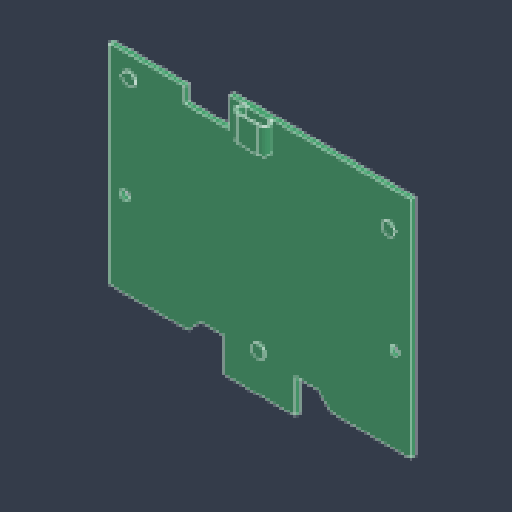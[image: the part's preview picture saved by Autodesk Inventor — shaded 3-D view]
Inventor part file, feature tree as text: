
AUTODESK INVENTOR PART (.ipt)
format: ipt  version: 2023.4 (Build 274418000, 418)  size: 162,816 bytes
history: native  units: mm
features: sketch x4, extrude x3, hole x1
ambient origin geometry x8: Origin, YZ Plane, XZ Plane, XY Plane, X Axis, Y Axis, Z Axis, Center Point
bodies: Solid1 (feature_tree)
feature tree (8):
  extrude  "Extrusion1"  Depth=65.0mm
  hole  "Hole1"  [1 undecoded]
  extrude  "Extrusion2"  Depth=3.5mm
  extrude  "Extrusion3"  TaperAngle=45.0deg  [1 undecoded]
  sketch  "Sketch1"  dims[d0=80.0mm d1=65.0mm]
  sketch  "Sketch2"  dims[d2=19.0mm d3=45.0deg]
  sketch  "Sketch4"  dims[d4=9.0mm d5=3.5mm]
  sketch  "Sketch5"  dims[d6=6.0mm d7=45.0deg d8=8.0mm d9=8.0mm d10=12.0mm d11=4.0mm d12=1.3mm d13=0.0mm d14=71.4mm d15=22.7mm d16=2.5mm d17=6.0mm d18=40.0mm d19=25.5mm d20=90.0deg d21=8.0mm d22=20.594885mm d23=3.2mm d24=9.0mm d25=0.4mm d26=6.8mm d27=0.0mm d28=3.4mm d29=68.8mm d30=27.4mm d31=18.0mm d32=0.4mm d33=0.0mm]
note: 2 required parameter values undecoded (feature->parameter linkage not recoverable at this tier; creation-order binding heuristic only, values carry confidence <= 0.55)
